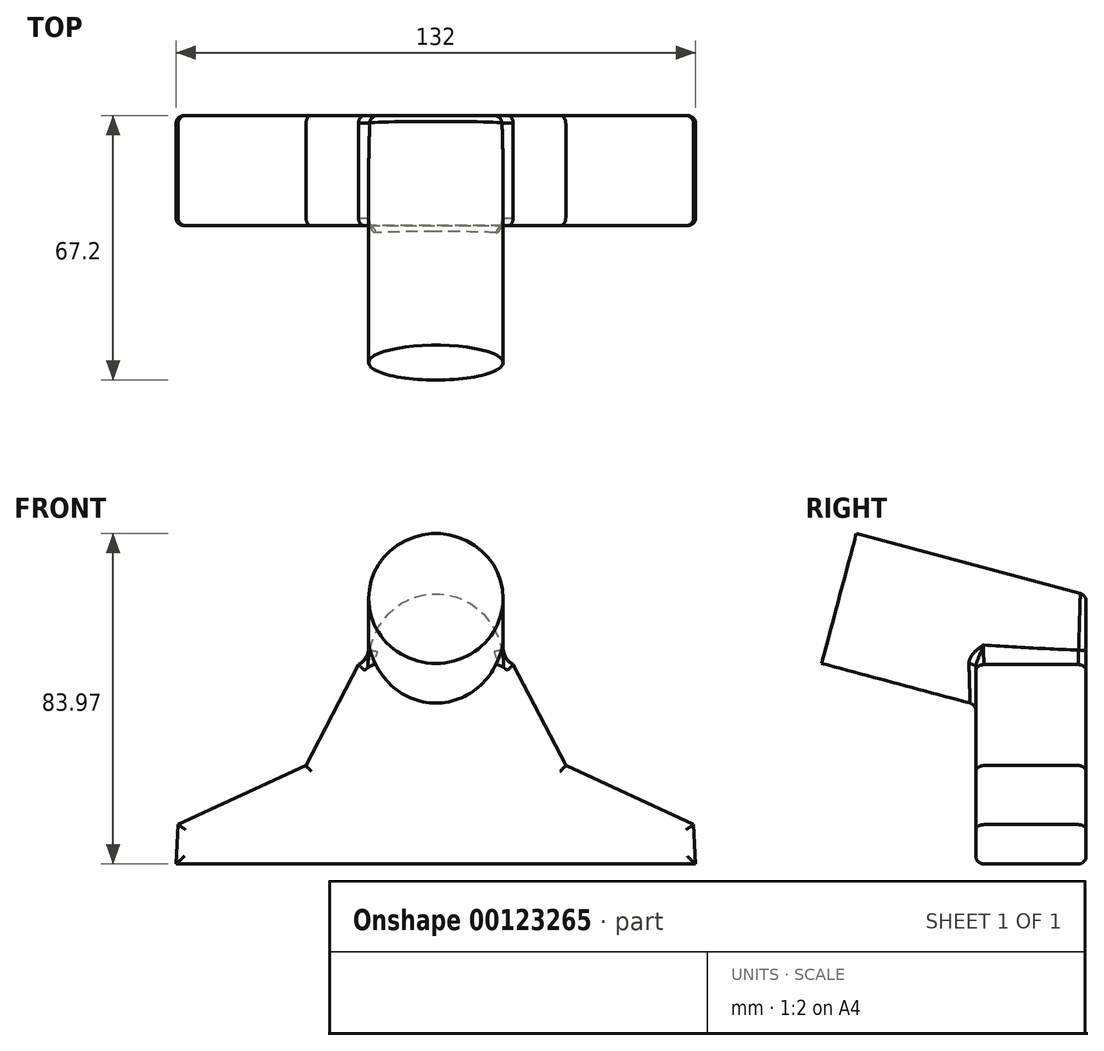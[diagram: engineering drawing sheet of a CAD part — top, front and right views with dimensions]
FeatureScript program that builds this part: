
annotation { "Feature Type Name" : "Feature", "Feature Type Description" : "" }
export const myFeature = defineFeature(function(context is Context, id is Id, definition is map)
    precondition{}
    {
        {
            var Q0;
            Q0=qCreatedBy(makeId("Front.planeOp"),FACE);
            var sketch = newSketch(context, id + "F0", { "sketchPlane" : qUnion([Q0])});
            skLineSegment(sketch, "E0", {"start": v(0, 0) * mm, "end": v(0, 5) * mm});
            skLineSegment(sketch, "E1", {"start": v(0, 5) * mm, "end": v(19.65, 5) * mm});
            skLineSegment(sketch, "E2", {"start": v(19.65, 5) * mm, "end": v(33, -20.65) * mm});
            skLineSegment(sketch, "E3", {"start": v(33, -20.65) * mm, "end": v(65.48, -35.65) * mm});
            skLineSegment(sketch, "E4", {"start": v(65.48, -35.65) * mm, "end": v(66, -45.65) * mm});
            skLineSegment(sketch, "E5", {"start": v(66, -45.65) * mm, "end": v(0, -45.65) * mm});
            skLineSegment(sketch, "E6", {"start": v(0, -45.65) * mm, "end": v(0, 0) * mm});
            skSolve(sketch);
        }
        {
            var Q0;
            Q0 = qSketchRegion(id + "F0", true);
            extrude(context, id + "F1", {"entities" : qUnion([Q0]), "oppositeDirection" : true, "depth" : 28 * mm});
        }
        {
            var Q0;
            Q0=makeQuery(id+"F1.opExtrude","SWEPT_BODY",BODY,{"disambiguationData":[OSD([sQuery(id+"F0.wireOp",EDGE,"E0"),sQuery(id+"F0.wireOp",EDGE,"E1"),sQuery(id+"F0.wireOp",EDGE,"E2"),sQuery(id+"F0.wireOp",EDGE,"E3"),sQuery(id+"F0.wireOp",EDGE,"E4"),sQuery(id+"F0.wireOp",EDGE,"E5"),sQuery(id+"F0.wireOp",EDGE,"E6")])]});
            var Q1;
            Q1=qCreatedBy(makeId("Right.planeOp"),FACE);
            mirror(context, id + "F2", {"operationType" : NewBodyOperationType.ADD, "entities" : qUnion([Q0]), "mirrorPlane" : qUnion([Q1])});
        }
        {
            var Q0;
            {var subQ0=makeQuery(id+"F1.opExtrude","CAP_EDGE",EDGE,{"disambiguationData":[OSD([sQuery(id+"F0.wireOp",EDGE,"E1")])],"isStart":false});Q0=makeQuery(id+"F2.boolean.opBoolean","MERGE",EDGE,{"derivedFrom":[subQ0,makeQuery(id+"F2.opPattern","COPY",EDGE,{"derivedFrom":subQ0,"instanceName":"1"})]});}
            cPlane(context, id + "F3", {"entities" : qUnion([Q0]), "cplaneType" : CPlaneType.LINE_ANGLE, "offset" : 25 * mm, "angle" : 165 * degree, "width" : 150 * mm, "height" : 150 * mm});
        }
        {
            var Q0;
            Q0=qCreatedBy(id+"F3.planeOp",FACE);
            cPlane(context, id + "F4", {"entities" : qUnion([Q0]), "cplaneType" : CPlaneType.OFFSET, "offset" : 65 * mm, "width" : 150 * mm, "height" : 150 * mm});
        }
        {
            var Q0;
            Q0=qCreatedBy(id+"F4.planeOp",FACE);
            var sketch = newSketch(context, id + "F5", { "sketchPlane" : qUnion([Q0])});
            skCircle(sketch, "E7", {"center": v(0, 12.08) * mm, "radius": 17.08 * mm});
            skSolve(sketch);
        }
        {
            var Q0;
            Q0=makeQuery(id+"F5.imprint","IMPRINT",FACE,{"disambiguationData":[TD([[makeQuery(id+"F5.imprint","IMPRINT",EDGE,{"derivedFrom":sQuery(id+"F5.wireOp",EDGE,"E7")}),1.0]])]});
            var Q1;
            {var subQ0=makeQuery(id+"F1.opExtrude","CAP_FACE",FACE,{"disambiguationData":[OSD([sQuery(id+"F0.wireOp",EDGE,"E0"),sQuery(id+"F0.wireOp",EDGE,"E1"),sQuery(id+"F0.wireOp",EDGE,"E2"),sQuery(id+"F0.wireOp",EDGE,"E3"),sQuery(id+"F0.wireOp",EDGE,"E4"),sQuery(id+"F0.wireOp",EDGE,"E5"),sQuery(id+"F0.wireOp",EDGE,"E6")])],"isStart":false});Q1=makeQuery(id+"F2.boolean.opBoolean","MERGE",FACE,{"derivedFrom":[subQ0,makeQuery(id+"F2.opPattern","COPY",FACE,{"derivedFrom":subQ0,"instanceName":"1"})]});}
            extrude(context, id + "F6", {"entities" : qUnion([Q0]), "operationType" : NewBodyOperationType.ADD, "endBound" : BoundingType.UP_TO_SURFACE, "oppositeDirection" : true, "endBoundEntityFace" : qUnion([Q1]), "depth" : 25 * mm});
        }
        {
            var Q0;
            {var subQ0=makeQuery(id+"F1.opExtrude","SWEPT_FACE",FACE,{"disambiguationData":[OSD([sQuery(id+"F0.wireOp",EDGE,"E1")])]});Q0=makeQuery(id+"F6.boolean.opBoolean","INTERSECT",EDGE,{"disambiguationData":[OD(0.0)],"derivedFrom":[makeQuery(id+"F2.boolean.opBoolean","MERGE",FACE,{"derivedFrom":[subQ0,makeQuery(id+"F2.opPattern","COPY",FACE,{"derivedFrom":subQ0,"instanceName":"1"})]}),makeQuery(id+"F6.opExtrude","SWEPT_FACE",FACE,{"disambiguationData":[OSD([sQuery(id+"F5.wireOp",EDGE,"E7")])]})]});}
            var Q1;
            {var subQ0=makeQuery(id+"F1.opExtrude","SWEPT_FACE",FACE,{"disambiguationData":[OSD([sQuery(id+"F0.wireOp",EDGE,"E1")])]});Q1=makeQuery(id+"F6.boolean.opBoolean","INTERSECT",EDGE,{"disambiguationData":[OD(1.0)],"derivedFrom":[makeQuery(id+"F2.boolean.opBoolean","MERGE",FACE,{"derivedFrom":[subQ0,makeQuery(id+"F2.opPattern","COPY",FACE,{"derivedFrom":subQ0,"instanceName":"1"})]}),makeQuery(id+"F6.opExtrude","SWEPT_FACE",FACE,{"disambiguationData":[OSD([sQuery(id+"F5.wireOp",EDGE,"E7")])]})]});}
            fillet(context, id + "F7", {"entities" : qUnion([Q0, Q1]), "radius" : 5 * mm, "tangentPropagation" : true, "allowEdgeOverflow" : false});
        }
        {
            var Q0;
            Q0=makeQuery(id+"F1.opExtrude","CAP_EDGE",EDGE,{"disambiguationData":[OSD([sQuery(id+"F0.wireOp",EDGE,"E4")])],"isStart":false});
            var Q1;
            {var subQ0=sQuery(id+"F0.wireOp",EDGE,"E6");var subQ1=sQuery(id+"F0.wireOp",EDGE,"E5");var subQ2=sQuery(id+"F0.wireOp",EDGE,"E4");var subQ3=sQuery(id+"F0.wireOp",EDGE,"E3");var subQ4=sQuery(id+"F0.wireOp",EDGE,"E2");var subQ5=sQuery(id+"F0.wireOp",EDGE,"E1");var subQ6=sQuery(id+"F0.wireOp",EDGE,"E0");var subQ7=makeQuery(id+"F1.opExtrude","CAP_FACE",FACE,{"disambiguationData":[OSD([subQ6,subQ5,subQ4,subQ3,subQ2,subQ1,subQ0])],"isStart":false});Q1=makeQuery(id+"F6.boolean.opBoolean","MERGE",FACE,{"derivedFrom":[makeQuery(id+"F2.boolean.opBoolean","MERGE",FACE,{"derivedFrom":[subQ7,makeQuery(id+"F2.opPattern","COPY",FACE,{"derivedFrom":subQ7,"instanceName":"1"})]}),makeQuery(id+"F6.opExtrude","CAP_FACE",FACE,{"disambiguationData":[OSD([subQ6,subQ5,subQ4,subQ3,subQ2,subQ1,subQ0])],"isStart":false})]});}
            var Q2;
            {var subQ0=makeQuery(id+"F1.opExtrude","CAP_EDGE",EDGE,{"disambiguationData":[OSD([sQuery(id+"F0.wireOp",EDGE,"E5")])],"isStart":true});Q2=makeQuery(id+"F2.boolean.opBoolean","MERGE",EDGE,{"derivedFrom":[subQ0,makeQuery(id+"F2.opPattern","COPY",EDGE,{"derivedFrom":subQ0,"instanceName":"1"})]});}
            var Q3;
            {var subQ0=makeQuery(id+"F1.opExtrude","CAP_FACE",FACE,{"disambiguationData":[OSD([sQuery(id+"F0.wireOp",EDGE,"E0"),sQuery(id+"F0.wireOp",EDGE,"E1"),sQuery(id+"F0.wireOp",EDGE,"E2"),sQuery(id+"F0.wireOp",EDGE,"E3"),sQuery(id+"F0.wireOp",EDGE,"E4"),sQuery(id+"F0.wireOp",EDGE,"E5"),sQuery(id+"F0.wireOp",EDGE,"E6")])],"isStart":true});Q3=makeQuery(id+"F2.boolean.opBoolean","MERGE",FACE,{"derivedFrom":[subQ0,makeQuery(id+"F2.opPattern","COPY",FACE,{"derivedFrom":subQ0,"instanceName":"1"})]});}
            fillet(context, id + "F8", {"entities" : qUnion([Q0, Q1, Q2, Q3]), "radius" : 2 * mm, "tangentPropagation" : true, "allowEdgeOverflow" : false});
        }
    });
